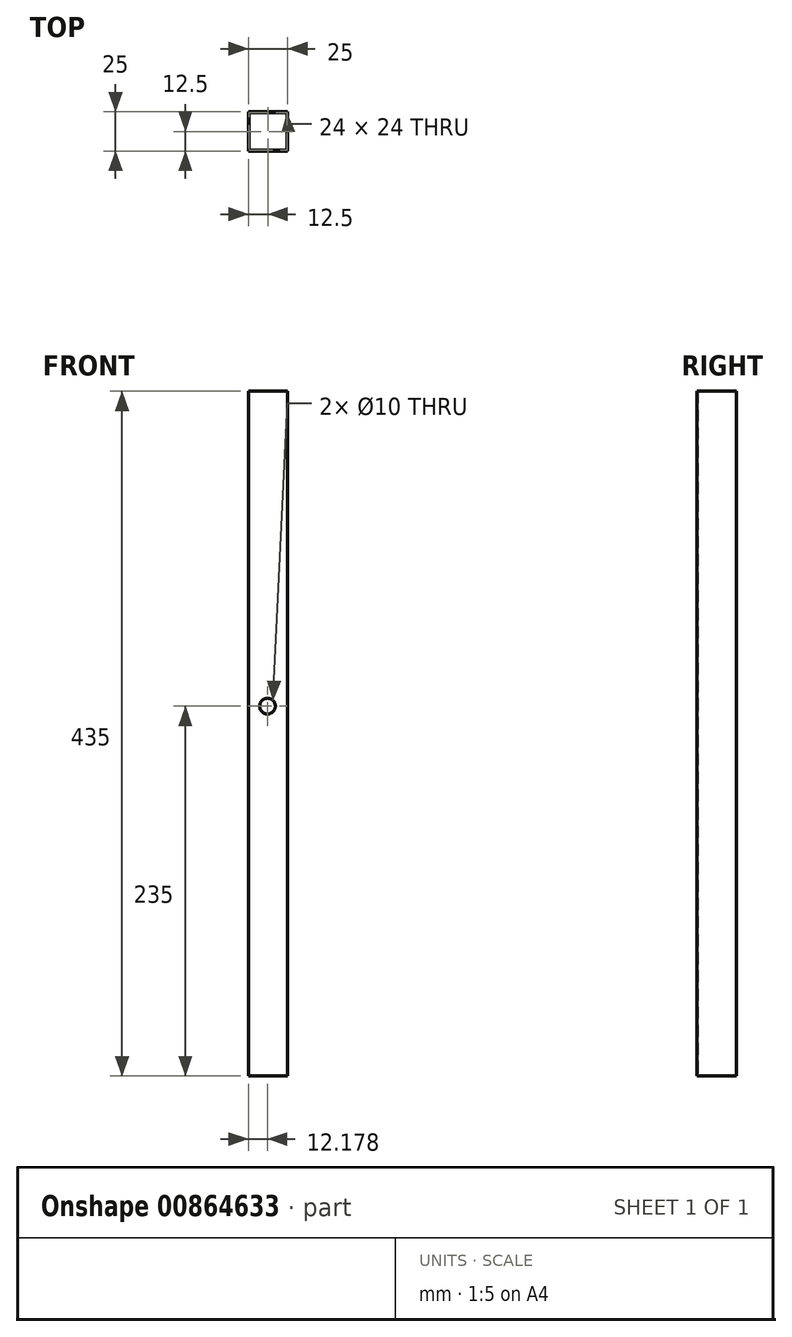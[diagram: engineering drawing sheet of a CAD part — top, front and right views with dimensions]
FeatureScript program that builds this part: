
annotation { "Feature Type Name" : "Feature", "Feature Type Description" : "" }
export const myFeature = defineFeature(function(context is Context, id is Id, definition is map)
    precondition{}
    {
        {
            var Q0;
            Q0=qCreatedBy(makeId("Top.planeOp"),FACE);
            var sketch = newSketch(context, id + "F0", { "sketchPlane" : qUnion([Q0])});
            skLineSegment(sketch, "E0.bottom", {"start": v(0, 0) * mm, "end": v(25, 0) * mm});
            skLineSegment(sketch, "E0.top", {"start": v(0, -25) * mm, "end": v(25, -25) * mm});
            skLineSegment(sketch, "E0.left", {"start": v(0, 0) * mm, "end": v(0, -25) * mm});
            skLineSegment(sketch, "E0.right", {"start": v(25, 0) * mm, "end": v(25, -25) * mm});
            skLineSegment(sketch, "E1.bottom", {"start": v(0.5, -0.5) * mm, "end": v(24.5, -0.5) * mm});
            skLineSegment(sketch, "E1.top", {"start": v(0.5, -24.5) * mm, "end": v(24.5, -24.5) * mm});
            skLineSegment(sketch, "E1.left", {"start": v(0.5, -0.5) * mm, "end": v(0.5, -24.5) * mm});
            skLineSegment(sketch, "E1.right", {"start": v(24.5, -0.5) * mm, "end": v(24.5, -24.5) * mm});
            skSolve(sketch);
        }
        {
            var Q0;
            Q0 = qSketchRegion(id + "F0", true);
            extrude(context, id + "F1", {"entities" : qUnion([Q0]), "depth" : 435 * mm, "offsetDistance" : 25 * mm});
        }
        {
            var Q0;
            Q0=makeQuery(id+"F1.opExtrude","SWEPT_FACE",FACE,{"disambiguationData":[OSD([sQuery(id+"F0.wireOp",EDGE,"E0.top")])]});
            var sketch = newSketch(context, id + "F2", { "sketchPlane" : qUnion([Q0])});
            skCircle(sketch, "E2", {"center": v(12.18, 235) * mm, "radius": 5 * mm});
            skLineSegment(sketch, "E3", {"start": v(12.5, 435) * mm, "end": v(12.18, 0) * mm});
            skSolve(sketch);
        }
        {
            var Q0;
            Q0 = qSketchRegion(id + "F2", true);
            extrude(context, id + "F3", {"entities" : qUnion([Q0]), "operationType" : NewBodyOperationType.REMOVE, "endBound" : BoundingType.THROUGH_ALL, "oppositeDirection" : true, "depth" : 25 * mm, "offsetDistance" : 25 * mm});
        }
    });
